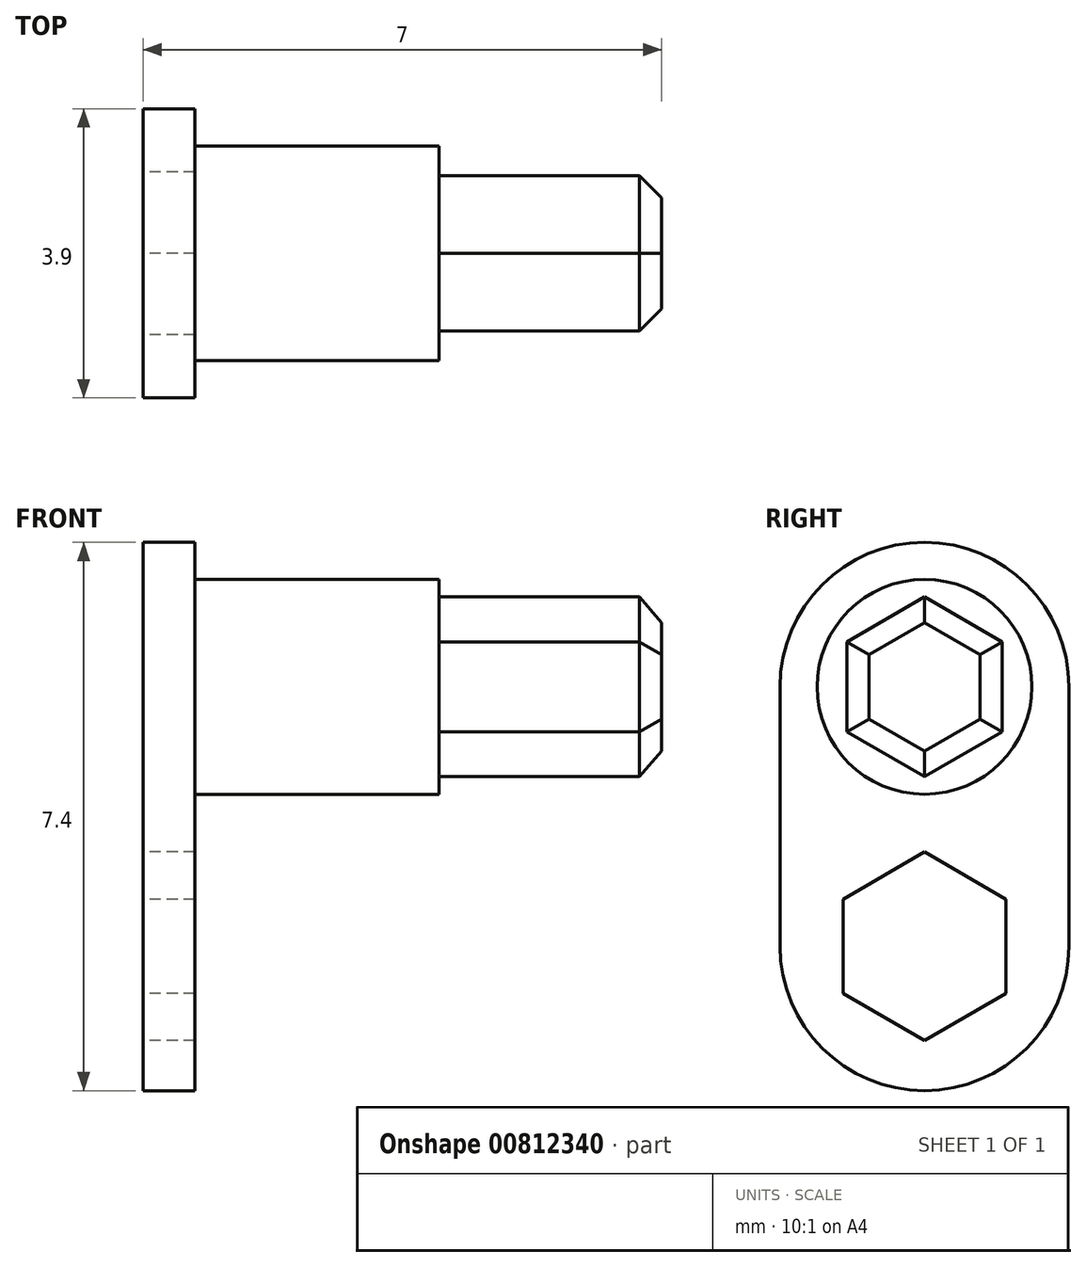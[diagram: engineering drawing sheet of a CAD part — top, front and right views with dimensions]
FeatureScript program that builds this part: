
annotation { "Feature Type Name" : "Feature", "Feature Type Description" : "" }
export const myFeature = defineFeature(function(context is Context, id is Id, definition is map)
    precondition{}
    {
        {
            var Q0;
            Q0=qCreatedBy(makeId("Right.planeOp"),FACE);
            var sketch = newSketch(context, id + "F0", { "sketchPlane" : qUnion([Q0])});
            skLineSegment(sketch, "E0.bottom", {"start": v(1.95, 1.75) * mm, "end": v(-1.95, 1.75) * mm});
            skLineSegment(sketch, "E0.top", {"start": v(1.95, -1.75) * mm, "end": v(-1.95, -1.75) * mm});
            skLineSegment(sketch, "E0.left", {"start": v(1.95, 1.75) * mm, "end": v(1.95, -1.75) * mm});
            skLineSegment(sketch, "E0.right", {"start": v(-1.95, 1.75) * mm, "end": v(-1.95, -1.75) * mm});
            skPoint(sketch, "E0.middle", {"position": v(0, 0) * mm});
            skArc(sketch, "E1", {"start": v(-1.95, 1.75) * mm, "mid": v(0, 3.7) * mm, "end": v(1.95, 1.75) * mm});
            skArc(sketch, "E2", {"start": v(-1.95, -1.75) * mm, "mid": v(0, -3.7) * mm, "end": v(1.95, -1.75) * mm});
            skSolve(sketch);
        }
        {
            var Q0;
            Q0 = qSketchRegion(id + "F0", true);
            extrude(context, id + "F1", {"entities" : qUnion([Q0]), "depth" : .7 * mm, "offsetDistance" : 25 * mm});
        }
        {
            var Q0;
            Q0=qCreatedBy(makeId("Right.planeOp"),FACE);
            var sketch = newSketch(context, id + "F2", { "sketchPlane" : qUnion([Q0])});
            skCircle(sketch, "E3", {"center": v(0, 1.75) * mm, "radius": 1.45 * mm});
            skSolve(sketch);
        }
        {
            var Q0;
            Q0 = qSketchRegion(id + "F2", true);
            extrude(context, id + "F3", {"entities" : qUnion([Q0]), "operationType" : NewBodyOperationType.ADD, "depth" : 4 * mm, "offsetDistance" : 25 * mm});
        }
        {
            var Q0;
            Q0=makeQuery(id+"F3.opExtrude","CAP_FACE",FACE,{"disambiguationData":[OSD([sQuery(id+"F2.wireOp",EDGE,"E3")])],"isStart":false});
            var sketch = newSketch(context, id + "F4", { "sketchPlane" : qUnion([Q0])});
            skCircle(sketch, "E4.cCircle", {"center": v(0, 1.75) * mm, "radius": 1.05 * mm, "construction": true});
            skLineSegment(sketch, "E4.0", {"start": v(1.05, 2.36) * mm, "end": v(1.05, 1.14) * mm});
            skLineSegment(sketch, "E4.1", {"start": v(1.05, 1.14) * mm, "end": v(0, 0.54) * mm});
            skLineSegment(sketch, "E4.2", {"start": v(0, 0.54) * mm, "end": v(-1.05, 1.14) * mm});
            skLineSegment(sketch, "E4.3", {"start": v(-1.05, 1.14) * mm, "end": v(-1.05, 2.36) * mm});
            skLineSegment(sketch, "E4.4", {"start": v(-1.05, 2.36) * mm, "end": v(0, 2.96) * mm});
            skLineSegment(sketch, "E4.5", {"start": v(0, 2.96) * mm, "end": v(1.05, 2.36) * mm});
            skPoint(sketch, "E4.0.midPoint", {"position": v(1.05, 1.75) * mm});
            skSolve(sketch);
        }
        {
            var Q0;
            Q0 = qSketchRegion(id + "F4", true);
            extrude(context, id + "F5", {"entities" : qUnion([Q0]), "operationType" : NewBodyOperationType.ADD, "depth" : 3 * mm, "offsetDistance" : 25 * mm});
        }
        {
            var Q0;
            Q0=makeQuery(id+"F5.opExtrude","CAP_EDGE",EDGE,{"disambiguationData":[OSD([sQuery(id+"F4.wireOp",EDGE,"E4.4")])],"isStart":false});
            var Q1;
            Q1=makeQuery(id+"F5.opExtrude","CAP_EDGE",EDGE,{"disambiguationData":[OSD([sQuery(id+"F4.wireOp",EDGE,"E4.5")])],"isStart":false});
            var Q2;
            Q2=makeQuery(id+"F5.opExtrude","CAP_EDGE",EDGE,{"disambiguationData":[OSD([sQuery(id+"F4.wireOp",EDGE,"E4.0")])],"isStart":false});
            var Q3;
            Q3=makeQuery(id+"F5.opExtrude","CAP_EDGE",EDGE,{"disambiguationData":[OSD([sQuery(id+"F4.wireOp",EDGE,"E4.1")])],"isStart":false});
            var Q4;
            Q4=makeQuery(id+"F5.opExtrude","CAP_EDGE",EDGE,{"disambiguationData":[OSD([sQuery(id+"F4.wireOp",EDGE,"E4.2")])],"isStart":false});
            var Q5;
            Q5=makeQuery(id+"F5.opExtrude","CAP_EDGE",EDGE,{"disambiguationData":[OSD([sQuery(id+"F4.wireOp",EDGE,"E4.3")])],"isStart":false});
            chamfer(context, id + "F6", {"entities" : qUnion([Q0, Q1, Q2, Q3, Q4, Q5]), "width" : .3 * mm, "tangentPropagation" : true});
        }
        {
            var Q0;
            Q0=makeQuery(id+"F1.opExtrude","CAP_FACE",FACE,{"disambiguationData":[OSD([sQuery(id+"F0.wireOp",EDGE,"E0.left"),sQuery(id+"F0.wireOp",EDGE,"E0.right"),sQuery(id+"F0.wireOp",EDGE,"E1"),sQuery(id+"F0.wireOp",EDGE,"E2")])],"isStart":true});
            var sketch = newSketch(context, id + "F7", { "sketchPlane" : qUnion([Q0])});
            skCircle(sketch, "E5.cCircle", {"center": v(0, -1.75) * mm, "radius": 1.1 * mm, "construction": true});
            skLineSegment(sketch, "E5.0", {"start": v(1.1, -1.11) * mm, "end": v(1.1, -2.39) * mm});
            skLineSegment(sketch, "E5.1", {"start": v(1.1, -2.39) * mm, "end": v(0, -3.02) * mm});
            skLineSegment(sketch, "E5.2", {"start": v(0, -3.02) * mm, "end": v(-1.1, -2.39) * mm});
            skLineSegment(sketch, "E5.3", {"start": v(-1.1, -2.39) * mm, "end": v(-1.1, -1.11) * mm});
            skLineSegment(sketch, "E5.4", {"start": v(-1.1, -1.11) * mm, "end": v(0, -0.48) * mm});
            skLineSegment(sketch, "E5.5", {"start": v(0, -0.48) * mm, "end": v(1.1, -1.11) * mm});
            skPoint(sketch, "E5.0.midPoint", {"position": v(1.1, -1.75) * mm});
            skSolve(sketch);
        }
        {
            var Q0;
            Q0 = qSketchRegion(id + "F7", true);
            extrude(context, id + "F8", {"entities" : qUnion([Q0]), "operationType" : NewBodyOperationType.REMOVE, "endBound" : BoundingType.UP_TO_NEXT, "oppositeDirection" : true, "depth" : 25 * mm, "offsetDistance" : 25 * mm});
        }
    });
